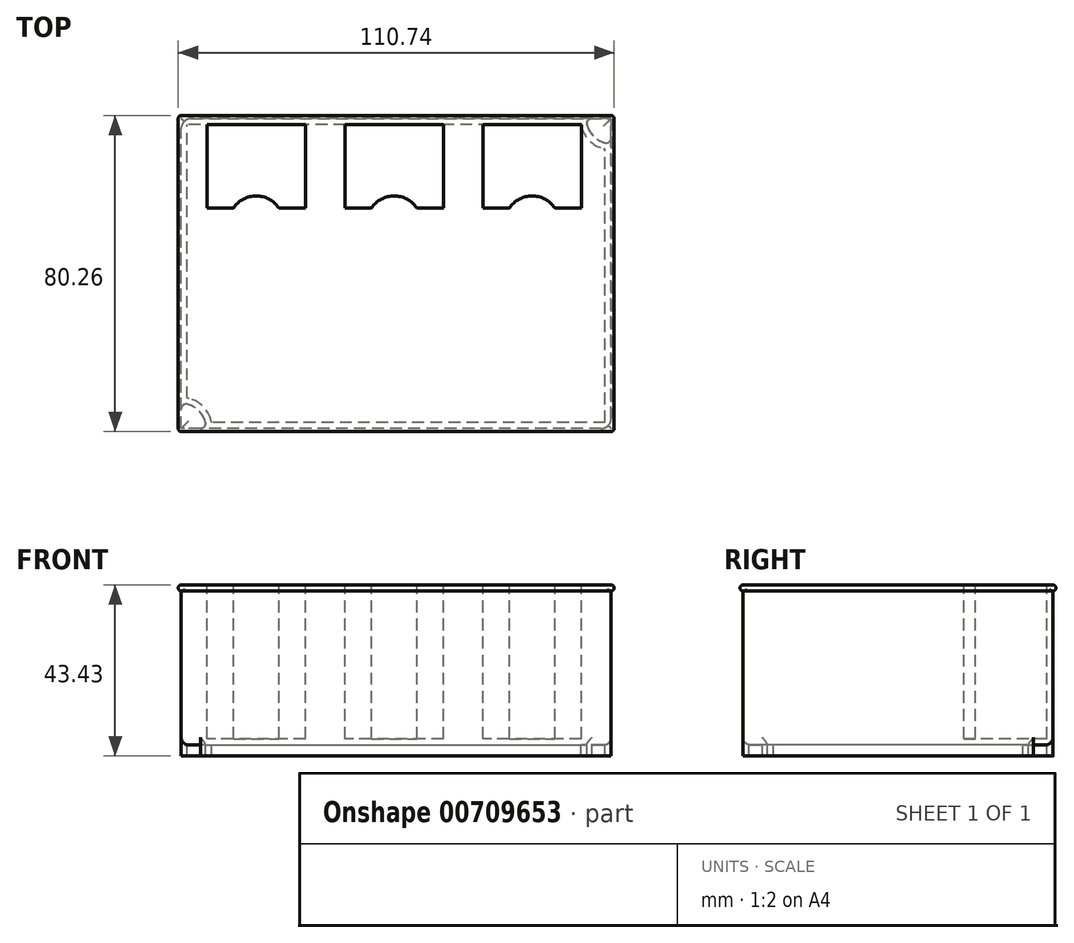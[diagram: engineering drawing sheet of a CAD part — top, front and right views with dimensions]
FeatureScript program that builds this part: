
annotation { "Feature Type Name" : "Feature", "Feature Type Description" : "" }
export const myFeature = defineFeature(function(context is Context, id is Id, definition is map)
    precondition{}
    {
        {
            var Q0;
            Q0=qCreatedBy(makeId("Front.planeOp"),FACE);
            var sketch = newSketch(context, id + "F0", { "sketchPlane" : qUnion([Q0])});
            skLineSegment(sketch, "E0.bottom", {"start": v(54.61, -20.32) * mm, "end": v(-54.61, -20.32) * mm});
            skLineSegment(sketch, "E0.top", {"start": v(54.61, 20.32) * mm, "end": v(-54.61, 20.32) * mm});
            skLineSegment(sketch, "E0.left", {"start": v(54.61, -20.32) * mm, "end": v(54.61, 20.32) * mm});
            skLineSegment(sketch, "E0.right", {"start": v(-54.61, -20.32) * mm, "end": v(-54.61, 20.32) * mm});
            skPoint(sketch, "E0.middle", {"position": v(0, 0) * mm});
            skSolve(sketch);
        }
        {
            var Q0;
            Q0=makeQuery(id+"F0.imprint","IMPRINT",FACE,{"disambiguationData":[TD([[makeQuery(id+"F0.imprint","IMPRINT",EDGE,{"derivedFrom":sQuery(id+"F0.wireOp",EDGE,"E0.bottom")}),-1.0]])]});
            extrude(context, id + "F1", {"entities" : qUnion([Q0]), "depth" : 78.74 * mm, "symmetric" : true});
        }
        {
            var Q0;
            Q0=makeQuery(id+"F1.opExtrude","SWEPT_FACE",FACE,{"disambiguationData":[OSD([sQuery(id+"F0.wireOp",EDGE,"E0.top")])]});
            shell(context, id + "F2", {"entities" : qUnion([Q0]), "thickness" : 1.52 * mm});
        }
        {
            var Q0;
            Q0=makeQuery(id+"F1.opExtrude","CAP_FACE",FACE,{"disambiguationData":[OSD([sQuery(id+"F0.wireOp",EDGE,"E0.bottom"),sQuery(id+"F0.wireOp",EDGE,"E0.top"),sQuery(id+"F0.wireOp",EDGE,"E0.left"),sQuery(id+"F0.wireOp",EDGE,"E0.right")])],"isStart":false});
            var sketch = newSketch(context, id + "F3", { "sketchPlane" : qUnion([Q0])});
            skArc(sketch, "E1", {"start": v(-54.61, 20.32) * mm, "mid": v(-55.37, 19.56) * mm, "end": v(-54.61, 18.8) * mm});
            skSolve(sketch);
        }
        {
            var Q0;
            {var subQ0=sQuery(id+"F3.wireOp",EDGE,"E1");Q0=makeQuery(id+"F3.imprint","IMPRINT",FACE,{"disambiguationData":[TD([[makeQuery(id+"F3.imprint","IMPRINT",EDGE,{"derivedFrom":subQ0}),1.0]])]});}
            var Q1;
            Q1=makeQuery(id+"F1.opExtrude","SWEPT_EDGE",EDGE,{"disambiguationData":[OSD([sQuery(id+"F0.wireOp",EDGE,"E0.top"),sQuery(id+"F0.wireOp",EDGE,"E0.right")])]});
            var Q2;
            Q2=makeQuery(id+"F1.opExtrude","CAP_EDGE",EDGE,{"disambiguationData":[OSD([sQuery(id+"F0.wireOp",EDGE,"E0.top")])],"isStart":true});
            var Q3;
            Q3=makeQuery(id+"F1.opExtrude","SWEPT_EDGE",EDGE,{"disambiguationData":[OSD([sQuery(id+"F0.wireOp",EDGE,"E0.top"),sQuery(id+"F0.wireOp",EDGE,"E0.left")])]});
            var Q4;
            Q4=makeQuery(id+"F1.opExtrude","CAP_EDGE",EDGE,{"disambiguationData":[OSD([sQuery(id+"F0.wireOp",EDGE,"E0.top")])],"isStart":false});
            sweep(context, id + "F4", {"operationType" : NewBodyOperationType.ADD, "profiles" : qUnion([Q0]), "path" : qUnion([Q1, Q2, Q3, Q4])});
        }
        {
            var Q0;
            Q0=makeQuery(id+"F1.opExtrude","SWEPT_FACE",FACE,{"disambiguationData":[OSD([sQuery(id+"F0.wireOp",EDGE,"E0.bottom")])]});
            var sketch = newSketch(context, id + "F5", { "sketchPlane" : qUnion([Q0])});
            skLineSegment(sketch, "E2.bottom", {"start": v(54.61, 39.37) * mm, "end": v(49.7, 39.37) * mm});
            skLineSegment(sketch, "E2.left", {"start": v(54.61, 39.37) * mm, "end": v(54.61, 34.45) * mm});
            skPoint(sketch, "E3.newPointA", {"position": v(48.26, 19.05) * mm});
            skArc(sketch, "E4", {"start": v(48.46, 37.78) * mm, "mid": v(50.12, 34.88) * mm, "end": v(53.02, 33.22) * mm});
            skPoint(sketch, "E5.visualSharp", {"position": v(48.26, 39.37) * mm});
            skArc(sketch, "E5.filletArc", {"start": v(49.7, 39.37) * mm, "mid": v(48.69, 38.88) * mm, "end": v(48.46, 37.78) * mm});
            skPoint(sketch, "E6.visualSharp", {"position": v(54.61, 33.02) * mm});
            skArc(sketch, "E6.filletArc", {"start": v(53.02, 33.22) * mm, "mid": v(54.12, 33.45) * mm, "end": v(54.6, 34.45) * mm});
            skArc(sketch, "E7.MirrorCS", {"start": v(-49.7, 39.37) * mm, "mid": v(-48.69, 38.88) * mm, "end": v(-48.46, 37.78) * mm});
            skArc(sketch, "E8.MirrorCS", {"start": v(-48.46, 37.78) * mm, "mid": v(-50.12, 34.88) * mm, "end": v(-53.02, 33.22) * mm});
            skArc(sketch, "E9.MirrorCS", {"start": v(-53.02, 33.22) * mm, "mid": v(-54.12, 33.45) * mm, "end": v(-54.6, 34.45) * mm});
            skLineSegment(sketch, "E10.MirrorCS", {"start": v(-54.61, 39.37) * mm, "end": v(-54.61, 34.45) * mm});
            skLineSegment(sketch, "E11.MirrorCS", {"start": v(-54.61, 39.37) * mm, "end": v(-49.7, 39.37) * mm});
            skArc(sketch, "E12.MirrorCS", {"start": v(-48.46, -37.78) * mm, "mid": v(-50.12, -34.88) * mm, "end": v(-53.02, -33.22) * mm});
            skArc(sketch, "E13.MirrorCS", {"start": v(-49.7, -39.37) * mm, "mid": v(-48.69, -38.88) * mm, "end": v(-48.46, -37.78) * mm});
            skLineSegment(sketch, "E14.MirrorCS", {"start": v(-54.6, -39.37) * mm, "end": v(-49.7, -39.37) * mm});
            skLineSegment(sketch, "E15.MirrorCS", {"start": v(-54.6, -39.37) * mm, "end": v(-54.6, -34.45) * mm});
            skArc(sketch, "E16.MirrorCS", {"start": v(-53.02, -33.22) * mm, "mid": v(-54.12, -33.45) * mm, "end": v(-54.6, -34.45) * mm});
            skArc(sketch, "E17.MirrorCS", {"start": v(49.7, -39.37) * mm, "mid": v(48.69, -38.88) * mm, "end": v(48.46, -37.78) * mm});
            skArc(sketch, "E18.MirrorCS", {"start": v(48.46, -37.78) * mm, "mid": v(50.12, -34.88) * mm, "end": v(53.02, -33.22) * mm});
            skArc(sketch, "E19.MirrorCS", {"start": v(53.02, -33.22) * mm, "mid": v(54.12, -33.45) * mm, "end": v(54.6, -34.45) * mm});
            skLineSegment(sketch, "E20.MirrorCS", {"start": v(54.6, -39.37) * mm, "end": v(54.6, -34.45) * mm});
            skLineSegment(sketch, "E21.MirrorCS", {"start": v(54.6, -39.37) * mm, "end": v(49.7, -39.37) * mm});
            skSolve(sketch);
        }
        {
            var Q0;
            Q0=makeQuery(id+"F5.imprint","IMPRINT",FACE,{"disambiguationData":[TD([[makeQuery(id+"F5.imprint","IMPRINT",EDGE,{"derivedFrom":sQuery(id+"F5.wireOp",EDGE,"E2.bottom")}),1.0]])]});
            var Q1;
            Q1=makeQuery(id+"F5.imprint","IMPRINT",FACE,{"disambiguationData":[TD([[makeQuery(id+"F5.imprint","IMPRINT",EDGE,{"derivedFrom":sQuery(id+"F5.wireOp",EDGE,"E8.MirrorCS")}),-1.0]])]});
            var Q2;
            Q2=makeQuery(id+"F5.imprint","IMPRINT",FACE,{"disambiguationData":[TD([[makeQuery(id+"F5.imprint","IMPRINT",EDGE,{"derivedFrom":sQuery(id+"F5.wireOp",EDGE,"E12.MirrorCS")}),1.0]])]});
            var Q3;
            Q3=makeQuery(id+"F5.imprint","IMPRINT",FACE,{"disambiguationData":[TD([[makeQuery(id+"F5.imprint","IMPRINT",EDGE,{"derivedFrom":sQuery(id+"F5.wireOp",EDGE,"E17.MirrorCS")}),-1.0]])]});
            extrude(context, id + "F6", {"entities" : qUnion([Q0, Q1, Q2, Q3]), "operationType" : NewBodyOperationType.ADD, "depth" : 2.8 * mm});
        }
        {
            var Q0;
            Q0=makeQuery(id+"F6.opExtrude","CAP_FACE",FACE,{"disambiguationData":[OSD([sQuery(id+"F5.wireOp",EDGE,"E2.bottom"),sQuery(id+"F5.wireOp",EDGE,"E2.left"),sQuery(id+"F5.wireOp",EDGE,"E4"),sQuery(id+"F5.wireOp",EDGE,"E5.filletArc"),sQuery(id+"F5.wireOp",EDGE,"E6.filletArc")])],"isStart":false});
            var Q1;
            Q1=makeQuery(id+"F6.opExtrude","CAP_FACE",FACE,{"disambiguationData":[OSD([sQuery(id+"F5.wireOp",EDGE,"E8.MirrorCS"),sQuery(id+"F5.wireOp",EDGE,"E9.MirrorCS"),sQuery(id+"F5.wireOp",EDGE,"E10.MirrorCS"),sQuery(id+"F5.wireOp",EDGE,"E7.MirrorCS"),sQuery(id+"F5.wireOp",EDGE,"E11.MirrorCS")])],"isStart":false});
            var Q2;
            Q2=makeQuery(id+"F6.opExtrude","CAP_FACE",FACE,{"disambiguationData":[OSD([sQuery(id+"F5.wireOp",EDGE,"E12.MirrorCS"),sQuery(id+"F5.wireOp",EDGE,"E13.MirrorCS"),sQuery(id+"F5.wireOp",EDGE,"E14.MirrorCS"),sQuery(id+"F5.wireOp",EDGE,"E15.MirrorCS"),sQuery(id+"F5.wireOp",EDGE,"E16.MirrorCS")])],"isStart":false});
            var Q3;
            Q3=makeQuery(id+"F6.opExtrude","CAP_FACE",FACE,{"disambiguationData":[OSD([sQuery(id+"F5.wireOp",EDGE,"E17.MirrorCS"),sQuery(id+"F5.wireOp",EDGE,"E18.MirrorCS"),sQuery(id+"F5.wireOp",EDGE,"E19.MirrorCS"),sQuery(id+"F5.wireOp",EDGE,"E20.MirrorCS"),sQuery(id+"F5.wireOp",EDGE,"E21.MirrorCS")])],"isStart":false});
            shell(context, id + "F7", {"entities" : qUnion([Q0, Q1, Q2, Q3]), "thickness" : 1.52 * mm});
        }
        {
            var Q0;
            Q0=makeQuery(id+"F1.opExtrude","SWEPT_EDGE",EDGE,{"disambiguationData":[OSD([sQuery(id+"F0.wireOp",EDGE,"E0.bottom"),sQuery(id+"F0.wireOp",EDGE,"E0.right")])]});
            var Q1;
            Q1=makeQuery(id+"F1.opExtrude","CAP_EDGE",EDGE,{"disambiguationData":[OSD([sQuery(id+"F0.wireOp",EDGE,"E0.bottom")])],"isStart":false});
            var Q2;
            Q2=makeQuery(id+"F1.opExtrude","SWEPT_EDGE",EDGE,{"disambiguationData":[OSD([sQuery(id+"F0.wireOp",EDGE,"E0.bottom"),sQuery(id+"F0.wireOp",EDGE,"E0.left")])]});
            var Q3;
            Q3=makeQuery(id+"F1.opExtrude","CAP_EDGE",EDGE,{"disambiguationData":[OSD([sQuery(id+"F0.wireOp",EDGE,"E0.bottom")])],"isStart":true});
            fillet(context, id + "F8", {"entities" : qUnion([Q0, Q1, Q2, Q3]), "radius" : 1.9 * mm, "tangentPropagation" : true, "allowEdgeOverflow" : false});
        }
        {
            var Q0;
            Q0=makeQuery(id+"F4.opSweep","MID_CAP_EDGE",EDGE,{"disambiguationData":[OSD([sQuery(id+"F0.wireOp",EDGE,"E0.top"),sQuery(id+"F0.wireOp",EDGE,"E0.left"),sQuery(id+"F3.wireOp",EDGE,"E1")])],"capPos":3.0});
            var Q1;
            Q1=makeQuery(id+"F4.opSweep","MID_CAP_EDGE",EDGE,{"disambiguationData":[OSD([sQuery(id+"F0.wireOp",EDGE,"E0.top"),sQuery(id+"F0.wireOp",EDGE,"E0.left"),sQuery(id+"F3.wireOp",EDGE,"E1")])],"capPos":2.0});
            var Q2;
            Q2=makeQuery(id+"F4.opSweep","MID_CAP_EDGE",EDGE,{"disambiguationData":[OSD([sQuery(id+"F0.wireOp",EDGE,"E0.top"),sQuery(id+"F0.wireOp",EDGE,"E0.right"),sQuery(id+"F3.wireOp",EDGE,"E1")])],"capPos":1.0});
            var Q3;
            Q3=makeQuery(id+"F4.opSweep","CAP_EDGE",EDGE,{"disambiguationData":[OSD([sQuery(id+"F0.wireOp",EDGE,"E0.top"),sQuery(id+"F0.wireOp",EDGE,"E0.right"),sQuery(id+"F3.wireOp",EDGE,"E1")])],"isStart":true});
            fillet(context, id + "F9", {"entities" : qUnion([Q0, Q1, Q2, Q3]), "radius" : 0.76 * mm, "tangentPropagation" : true, "allowEdgeOverflow" : false});
        }
        {
            var Q0;
            Q0=makeQuery(id+"F6.boolean.opBoolean","MERGE",EDGE,{"derivedFrom":[makeQuery(id+"F1.opExtrude","CAP_EDGE",EDGE,{"disambiguationData":[OSD([sQuery(id+"F0.wireOp",EDGE,"E0.left")])],"isStart":false}),makeQuery(id+"F6.opExtrude","SWEPT_EDGE",EDGE,{"disambiguationData":[OSD([sQuery(id+"F5.wireOp",EDGE,"E2.bottom"),sQuery(id+"F5.wireOp",EDGE,"E2.left")])]})]});
            var Q1;
            Q1=makeQuery(id+"F6.boolean.opBoolean","MERGE",EDGE,{"derivedFrom":[makeQuery(id+"F1.opExtrude","CAP_EDGE",EDGE,{"disambiguationData":[OSD([sQuery(id+"F0.wireOp",EDGE,"E0.left")])],"isStart":true}),makeQuery(id+"F6.opExtrude","SWEPT_EDGE",EDGE,{"disambiguationData":[OSD([sQuery(id+"F5.wireOp",EDGE,"E20.MirrorCS"),sQuery(id+"F5.wireOp",EDGE,"E21.MirrorCS")])]})]});
            var Q2;
            Q2=makeQuery(id+"F6.boolean.opBoolean","MERGE",EDGE,{"derivedFrom":[makeQuery(id+"F1.opExtrude","CAP_EDGE",EDGE,{"disambiguationData":[OSD([sQuery(id+"F0.wireOp",EDGE,"E0.right")])],"isStart":false}),makeQuery(id+"F6.opExtrude","SWEPT_EDGE",EDGE,{"disambiguationData":[OSD([sQuery(id+"F5.wireOp",EDGE,"E10.MirrorCS"),sQuery(id+"F5.wireOp",EDGE,"E11.MirrorCS")])]})]});
            var Q3;
            Q3=makeQuery(id+"F6.boolean.opBoolean","MERGE",EDGE,{"derivedFrom":[makeQuery(id+"F1.opExtrude","CAP_EDGE",EDGE,{"disambiguationData":[OSD([sQuery(id+"F0.wireOp",EDGE,"E0.right")])],"isStart":true}),makeQuery(id+"F6.opExtrude","SWEPT_EDGE",EDGE,{"disambiguationData":[OSD([sQuery(id+"F5.wireOp",EDGE,"E14.MirrorCS"),sQuery(id+"F5.wireOp",EDGE,"E15.MirrorCS")])]})]});
            fillet(context, id + "F10", {"entities" : qUnion([Q0, Q1, Q2, Q3]), "radius" : 2.54 * mm, "tangentPropagation" : true, "allowEdgeOverflow" : false});
        }
        {
            var Q0;
            Q0=makeQuery(id+"F1.opExtrude","SWEPT_FACE",FACE,{"disambiguationData":[OSD([sQuery(id+"F0.wireOp",EDGE,"E0.top")])]});
            var sketch = newSketch(context, id + "F11", { "sketchPlane" : qUnion([Q0])});
            skLineSegment(sketch, "E22.0", {"start": v(-53.09, -12.45) * mm, "end": v(-53.09, 37.85) * mm});
            skLineSegment(sketch, "E22.1", {"start": v(-53.09, 37.85) * mm, "end": v(-18.03, 37.85) * mm});
            skLineSegment(sketch, "E23", {"start": v(-18.03, 37.85) * mm, "end": v(-23.03, 37.85) * mm});
            skLineSegment(sketch, "E24", {"start": v(-23.03, 37.85) * mm, "end": v(-23.03, 16.7) * mm});
            skLineSegment(sketch, "E25", {"start": v(-53.09, 37.85) * mm, "end": v(-48.09, 37.85) * mm});
            skLineSegment(sketch, "E26", {"start": v(-48.09, 37.85) * mm, "end": v(-48.09, 16.7) * mm});
            skLineSegment(sketch, "E27.left", {"start": v(-23.03, 16.7) * mm, "end": v(-29.82, 16.7) * mm});
            skLineSegment(sketch, "E27.right", {"start": v(-23.03, 8.7) * mm, "end": v(-29.82, 8.7) * mm});
            skPoint(sketch, "E27.middle", {"position": v(-35.56, 12.7) * mm});
            skArc(sketch, "E28", {"start": v(-29.82, 16.7) * mm, "mid": v(-35.56, 19.7) * mm, "end": v(-41.3, 16.7) * mm});
            skLineSegment(sketch, "E29.bottom", {"start": v(-33.31, -0.3) * mm, "end": v(-33.31, 6.07) * mm});
            skLineSegment(sketch, "E29.top", {"start": v(-37.81, -0.3) * mm, "end": v(-37.81, 6.07) * mm});
            skLineSegment(sketch, "E29.left", {"start": v(-33.31, -0.3) * mm, "end": v(-37.81, -0.3) * mm});
            skLineSegment(sketch, "E30.trimOffspring", {"start": v(-41.3, 8.7) * mm, "end": v(-47.07, 8.7) * mm});
            skLineSegment(sketch, "E31.trimOffspring", {"start": v(-41.3, 16.7) * mm, "end": v(-48.09, 16.7) * mm});
            skArc(sketch, "E32.trimOffspring", {"start": v(-41.3, 8.7) * mm, "mid": v(-39.77, 7.1) * mm, "end": v(-37.81, 6.07) * mm});
            skLineSegment(sketch, "E33.trimOffspring", {"start": v(-23.03, 8.7) * mm, "end": v(-23.03, -8.7) * mm});
            skArc(sketch, "E34.trimOffspring", {"start": v(-33.31, 6.07) * mm, "mid": v(-31.35, 7.1) * mm, "end": v(-29.82, 8.7) * mm});
            skPoint(sketch, "E35", {"position": v(-20.53, -12.45) * mm});
            skLineSegment(sketch, "E36.1", {"start": v(-18.03, 37.85) * mm, "end": v(17.02, 37.85) * mm});
            skLineSegment(sketch, "E37", {"start": v(17.02, 37.85) * mm, "end": v(12.02, 37.85) * mm});
            skLineSegment(sketch, "E38", {"start": v(12.02, 37.85) * mm, "end": v(12.02, 16.7) * mm});
            skLineSegment(sketch, "E39", {"start": v(-18.03, 37.85) * mm, "end": v(-13.03, 37.85) * mm});
            skLineSegment(sketch, "E40", {"start": v(-13.03, 37.85) * mm, "end": v(-13.03, 16.7) * mm});
            skLineSegment(sketch, "E41.left", {"start": v(12.02, 16.7) * mm, "end": v(5.24, 16.7) * mm});
            skLineSegment(sketch, "E41.right", {"start": v(12.02, 8.7) * mm, "end": v(5.24, 8.7) * mm});
            skPoint(sketch, "E41.middle", {"position": v(-0.5, 12.7) * mm});
            skArc(sketch, "E42", {"start": v(5.24, 16.7) * mm, "mid": v(-0.5, 19.7) * mm, "end": v(-6.25, 16.7) * mm});
            skLineSegment(sketch, "E43.bottom", {"start": v(1.74, -0.3) * mm, "end": v(1.74, 6.07) * mm});
            skLineSegment(sketch, "E43.top", {"start": v(-2.76, -0.3) * mm, "end": v(-2.76, 6.07) * mm});
            skLineSegment(sketch, "E43.left", {"start": v(1.74, -0.3) * mm, "end": v(-2.76, -0.3) * mm});
            skLineSegment(sketch, "E44.trimOffspring", {"start": v(-6.25, 8.7) * mm, "end": v(-12.02, 8.7) * mm});
            skLineSegment(sketch, "E45.trimOffspring", {"start": v(-6.25, 16.7) * mm, "end": v(-13.03, 16.7) * mm});
            skArc(sketch, "E46.trimOffspring", {"start": v(-6.25, 8.7) * mm, "mid": v(-4.72, 7.1) * mm, "end": v(-2.76, 6.07) * mm});
            skLineSegment(sketch, "E47.trimOffspring", {"start": v(12.02, 8.7) * mm, "end": v(12.02, -8.7) * mm});
            skArc(sketch, "E48.trimOffspring", {"start": v(1.74, 6.07) * mm, "mid": v(3.7, 7.1) * mm, "end": v(5.24, 8.7) * mm});
            skPoint(sketch, "E49", {"position": v(14.52, -12.45) * mm});
            skLineSegment(sketch, "E50.1", {"start": v(17.02, 37.85) * mm, "end": v(52.07, 37.85) * mm});
            skLineSegment(sketch, "E50.2", {"start": v(52.07, 12.45) * mm, "end": v(52.07, 37.85) * mm});
            skLineSegment(sketch, "E51", {"start": v(52.07, 37.85) * mm, "end": v(47.07, 37.85) * mm});
            skLineSegment(sketch, "E52", {"start": v(47.07, 37.85) * mm, "end": v(47.07, 16.7) * mm});
            skLineSegment(sketch, "E53", {"start": v(17.02, 37.85) * mm, "end": v(22.02, 37.85) * mm});
            skLineSegment(sketch, "E54", {"start": v(22.02, 37.85) * mm, "end": v(22.02, 16.7) * mm});
            skLineSegment(sketch, "E55.left", {"start": v(47.07, 16.7) * mm, "end": v(40.29, 16.7) * mm});
            skLineSegment(sketch, "E55.right", {"start": v(47.07, 8.7) * mm, "end": v(40.29, 8.7) * mm});
            skPoint(sketch, "E55.middle", {"position": v(34.54, 12.7) * mm});
            skArc(sketch, "E56", {"start": v(40.29, 16.7) * mm, "mid": v(34.54, 19.7) * mm, "end": v(28.8, 16.7) * mm});
            skLineSegment(sketch, "E57.bottom", {"start": v(36.8, -0.3) * mm, "end": v(36.8, 6.07) * mm});
            skLineSegment(sketch, "E57.top", {"start": v(32.3, -0.3) * mm, "end": v(32.3, 6.07) * mm});
            skLineSegment(sketch, "E57.left", {"start": v(36.8, -0.3) * mm, "end": v(32.3, -0.3) * mm});
            skLineSegment(sketch, "E58.trimOffspring", {"start": v(28.8, 8.7) * mm, "end": v(23.03, 8.7) * mm});
            skLineSegment(sketch, "E59.trimOffspring", {"start": v(28.8, 16.7) * mm, "end": v(22.02, 16.7) * mm});
            skArc(sketch, "E60.trimOffspring", {"start": v(28.8, 8.7) * mm, "mid": v(30.34, 7.1) * mm, "end": v(32.3, 6.07) * mm});
            skLineSegment(sketch, "E61.trimOffspring", {"start": v(47.07, 8.7) * mm, "end": v(47.07, -8.7) * mm});
            skArc(sketch, "E62.trimOffspring", {"start": v(36.8, 6.07) * mm, "mid": v(38.75, 7.1) * mm, "end": v(40.29, 8.7) * mm});
            skPoint(sketch, "E63", {"position": v(49.57, -12.45) * mm});
            skLineSegment(sketch, "E64.0", {"start": v(-52.07, -37.85) * mm, "end": v(-52.07, -12.45) * mm});
            skLineSegment(sketch, "E64.3", {"start": v(-52.07, -37.85) * mm, "end": v(-17.02, -37.85) * mm});
            skLineSegment(sketch, "E65", {"start": v(-47.07, 8.7) * mm, "end": v(-47.07, -8.7) * mm});
            skLineSegment(sketch, "E66.left", {"start": v(-23.03, -8.7) * mm, "end": v(-28.8, -8.7) * mm});
            skLineSegment(sketch, "E66.right", {"start": v(-22.02, -16.7) * mm, "end": v(-28.8, -16.7) * mm});
            skPoint(sketch, "E66.middle", {"position": v(-34.54, -12.7) * mm});
            skArc(sketch, "E67", {"start": v(-28.8, -8.7) * mm, "mid": v(-34.54, -5.7) * mm, "end": v(-40.29, -8.7) * mm});
            skLineSegment(sketch, "E68.bottom", {"start": v(-32.3, -25.7) * mm, "end": v(-32.3, -19.33) * mm});
            skLineSegment(sketch, "E68.top", {"start": v(-36.8, -25.7) * mm, "end": v(-36.8, -19.33) * mm});
            skLineSegment(sketch, "E68.left", {"start": v(-32.3, -25.7) * mm, "end": v(-36.8, -25.7) * mm});
            skLineSegment(sketch, "E69.trimOffspring", {"start": v(-40.29, -16.7) * mm, "end": v(-47.07, -16.7) * mm});
            skLineSegment(sketch, "E70.trimOffspring", {"start": v(-40.29, -8.7) * mm, "end": v(-47.07, -8.7) * mm});
            skArc(sketch, "E71.trimOffspring", {"start": v(-40.29, -16.7) * mm, "mid": v(-38.75, -18.3) * mm, "end": v(-36.8, -19.33) * mm});
            skLineSegment(sketch, "E72.trimOffspring", {"start": v(-47.07, -16.7) * mm, "end": v(-47.07, -37.85) * mm});
            skLineSegment(sketch, "E73.trimOffspring", {"start": v(-22.02, -16.7) * mm, "end": v(-22.02, -37.85) * mm});
            skArc(sketch, "E74.trimOffspring", {"start": v(-32.3, -19.33) * mm, "mid": v(-30.34, -18.3) * mm, "end": v(-28.8, -16.7) * mm});
            skLineSegment(sketch, "E75", {"start": v(-22.02, -37.85) * mm, "end": v(-17.02, -37.85) * mm});
            skPoint(sketch, "E76", {"position": v(-19.52, -37.85) * mm});
            skLineSegment(sketch, "E77.3", {"start": v(-17.02, -37.85) * mm, "end": v(18.03, -37.85) * mm});
            skLineSegment(sketch, "E78", {"start": v(-12.02, 8.7) * mm, "end": v(-12.02, -8.7) * mm});
            skLineSegment(sketch, "E79.left", {"start": v(12.02, -8.7) * mm, "end": v(6.25, -8.7) * mm});
            skLineSegment(sketch, "E79.right", {"start": v(13.03, -16.7) * mm, "end": v(6.25, -16.7) * mm});
            skPoint(sketch, "E79.middle", {"position": v(0.5, -12.7) * mm});
            skArc(sketch, "E80", {"start": v(6.25, -8.7) * mm, "mid": v(0.5, -5.7) * mm, "end": v(-5.24, -8.7) * mm});
            skLineSegment(sketch, "E81.bottom", {"start": v(2.76, -25.7) * mm, "end": v(2.76, -19.33) * mm});
            skLineSegment(sketch, "E81.top", {"start": v(-1.74, -25.7) * mm, "end": v(-1.74, -19.33) * mm});
            skLineSegment(sketch, "E81.left", {"start": v(2.76, -25.7) * mm, "end": v(-1.74, -25.7) * mm});
            skLineSegment(sketch, "E82.trimOffspring", {"start": v(-5.24, -16.7) * mm, "end": v(-12.02, -16.7) * mm});
            skLineSegment(sketch, "E83.trimOffspring", {"start": v(-5.24, -8.7) * mm, "end": v(-12.02, -8.7) * mm});
            skArc(sketch, "E84.trimOffspring", {"start": v(-5.24, -16.7) * mm, "mid": v(-3.7, -18.3) * mm, "end": v(-1.74, -19.33) * mm});
            skLineSegment(sketch, "E85.trimOffspring", {"start": v(-12.02, -16.7) * mm, "end": v(-12.02, -37.85) * mm});
            skLineSegment(sketch, "E86.trimOffspring", {"start": v(13.03, -16.7) * mm, "end": v(13.03, -37.85) * mm});
            skArc(sketch, "E87.trimOffspring", {"start": v(2.76, -19.33) * mm, "mid": v(4.72, -18.3) * mm, "end": v(6.25, -16.7) * mm});
            skLineSegment(sketch, "E88", {"start": v(13.03, -37.85) * mm, "end": v(18.03, -37.85) * mm});
            skPoint(sketch, "E89", {"position": v(15.53, -37.85) * mm});
            skLineSegment(sketch, "E90.2", {"start": v(53.09, -37.85) * mm, "end": v(53.09, 12.45) * mm});
            skLineSegment(sketch, "E90.3", {"start": v(18.03, -37.85) * mm, "end": v(53.09, -37.85) * mm});
            skLineSegment(sketch, "E91", {"start": v(53.09, 12.45) * mm, "end": v(52.07, 12.45) * mm});
            skLineSegment(sketch, "E92", {"start": v(23.03, 8.7) * mm, "end": v(23.03, -8.7) * mm});
            skLineSegment(sketch, "E93.left", {"start": v(47.07, -8.7) * mm, "end": v(41.3, -8.7) * mm});
            skLineSegment(sketch, "E93.right", {"start": v(48.09, -16.7) * mm, "end": v(41.3, -16.7) * mm});
            skPoint(sketch, "E93.middle", {"position": v(35.56, -12.7) * mm});
            skArc(sketch, "E94", {"start": v(41.3, -8.7) * mm, "mid": v(35.56, -5.7) * mm, "end": v(29.82, -8.7) * mm});
            skLineSegment(sketch, "E95.bottom", {"start": v(37.81, -25.7) * mm, "end": v(37.81, -19.33) * mm});
            skLineSegment(sketch, "E95.top", {"start": v(33.31, -25.7) * mm, "end": v(33.31, -19.33) * mm});
            skLineSegment(sketch, "E95.left", {"start": v(37.81, -25.7) * mm, "end": v(33.31, -25.7) * mm});
            skLineSegment(sketch, "E96.trimOffspring", {"start": v(29.82, -16.7) * mm, "end": v(23.03, -16.7) * mm});
            skLineSegment(sketch, "E97.trimOffspring", {"start": v(29.82, -8.7) * mm, "end": v(23.03, -8.7) * mm});
            skArc(sketch, "E98.trimOffspring", {"start": v(29.82, -16.7) * mm, "mid": v(31.35, -18.3) * mm, "end": v(33.31, -19.33) * mm});
            skLineSegment(sketch, "E99.trimOffspring", {"start": v(23.03, -16.7) * mm, "end": v(23.03, -37.85) * mm});
            skLineSegment(sketch, "E100.trimOffspring", {"start": v(48.09, -16.7) * mm, "end": v(48.09, -37.85) * mm});
            skArc(sketch, "E101.trimOffspring", {"start": v(37.81, -19.33) * mm, "mid": v(39.77, -18.3) * mm, "end": v(41.3, -16.7) * mm});
            skLineSegment(sketch, "E102", {"start": v(48.09, -37.85) * mm, "end": v(53.09, -37.85) * mm});
            skPoint(sketch, "E103", {"position": v(50.59, -37.85) * mm});
            skLineSegment(sketch, "E104", {"start": v(-53.09, -12.45) * mm, "end": v(-52.07, -12.45) * mm});
            skPoint(sketch, "E105.orphan", {"position": v(-48.09, 8.7) * mm});
            skPoint(sketch, "E106.orphan", {"position": v(22.02, 8.7) * mm});
            skPoint(sketch, "E107.orphan", {"position": v(48.09, -8.7) * mm});
            skPoint(sketch, "E108.orphan", {"position": v(13.03, -8.7) * mm});
            skPoint(sketch, "E109.orphan", {"position": v(-22.02, -8.7) * mm});
            skPoint(sketch, "E110.orphan", {"position": v(-13.03, 8.7) * mm});
            skSolve(sketch);
        }
        {
            var Q0;
            Q0=makeQuery(id+"F11.imprint","IMPRINT",FACE,{"disambiguationData":[TD([[makeQuery(id+"F11.imprint","IMPRINT",EDGE,{"derivedFrom":sQuery(id+"F11.wireOp",EDGE,"E22.1")}),1.0]])]});
            var Q1;
            Q1=makeQuery(id+"F11.imprint","IMPRINT",FACE,{"disambiguationData":[TD([[makeQuery(id+"F11.imprint","IMPRINT",EDGE,{"derivedFrom":sQuery(id+"F11.wireOp",EDGE,"E36.1")}),1.0]])]});
            var Q2;
            Q2=makeQuery(id+"F11.imprint","IMPRINT",FACE,{"disambiguationData":[TD([[makeQuery(id+"F11.imprint","IMPRINT",EDGE,{"derivedFrom":sQuery(id+"F11.wireOp",EDGE,"E50.1")}),1.0]])]});
            var Q3;
            Q3=makeQuery(id+"F11.imprint","IMPRINT",FACE,{"disambiguationData":[TD([[makeQuery(id+"F11.imprint","IMPRINT",EDGE,{"derivedFrom":sQuery(id+"F11.wireOp",EDGE,"E55.right")}),1.0]])]});
            var Q4;
            Q4=makeQuery(id+"F11.imprint","IMPRINT",FACE,{"disambiguationData":[TD([[makeQuery(id+"F11.imprint","IMPRINT",EDGE,{"derivedFrom":sQuery(id+"F11.wireOp",EDGE,"E93.right")}),1.0]])]});
            var Q5;
            Q5=makeQuery(id+"F11.imprint","IMPRINT",FACE,{"disambiguationData":[TD([[makeQuery(id+"F11.imprint","IMPRINT",EDGE,{"derivedFrom":sQuery(id+"F11.wireOp",EDGE,"E79.right")}),1.0]])]});
            var Q6;
            Q6=makeQuery(id+"F11.imprint","IMPRINT",FACE,{"disambiguationData":[TD([[makeQuery(id+"F11.imprint","IMPRINT",EDGE,{"derivedFrom":sQuery(id+"F11.wireOp",EDGE,"E41.right")}),1.0]])]});
            var Q7;
            Q7=makeQuery(id+"F11.imprint","IMPRINT",FACE,{"disambiguationData":[TD([[makeQuery(id+"F11.imprint","IMPRINT",EDGE,{"derivedFrom":sQuery(id+"F11.wireOp",EDGE,"E27.right")}),1.0]])]});
            var Q8;
            Q8=makeQuery(id+"F11.imprint","IMPRINT",FACE,{"disambiguationData":[TD([[makeQuery(id+"F11.imprint","IMPRINT",EDGE,{"derivedFrom":sQuery(id+"F11.wireOp",EDGE,"E66.right")}),1.0]])]});
            var Q9;
            {var subQ0=sQuery(id+"F11.wireOp",EDGE,"E50.2");Q9=makeQuery(id+"F11.imprint","IMPRINT",FACE,{"disambiguationData":[TD([[makeQuery(id+"F11.imprint","IMPRINT",EDGE,{"derivedFrom":subQ0}),-1.0]])]});}
            var Q10;
            {var subQ0=sQuery(id+"F11.wireOp",EDGE,"E64.0");Q10=makeQuery(id+"F11.imprint","IMPRINT",FACE,{"disambiguationData":[TD([[makeQuery(id+"F11.imprint","IMPRINT",EDGE,{"derivedFrom":subQ0}),1.0]])]});}
            var Q11;
            Q11=makeQuery(id+"F2.opShell","OFFSET_FACE",FACE,{"disambiguationData":[OSD([sQuery(id+"F0.wireOp",EDGE,"E0.bottom")])]});
            extrude(context, id + "F12", {"entities" : qUnion([Q0, Q1, Q2, Q3, Q4, Q5, Q6, Q7, Q8, Q9, Q10]), "operationType" : NewBodyOperationType.ADD, "endBound" : BoundingType.UP_TO_SURFACE, "oppositeDirection" : true, "depth" : 25 * mm, "endBoundEntityFace" : qUnion([Q11]), "offsetDistance" : 25 * mm});
        }
        {
            var Q0;
            {var subQ0=sQuery(id+"F0.wireOp",EDGE,"E0.top");Q0=makeQuery(id+"F12.boolean.opBoolean","MERGE",FACE,{"derivedFrom":[makeQuery(id+"F1.opExtrude","SWEPT_FACE",FACE,{"disambiguationData":[OSD([subQ0])]}),makeQuery(id+"F12.opExtrude","CAP_FACE",FACE,{"disambiguationData":[OSD([sQuery(id+"F11.wireOp",EDGE,"E22.1"),sQuery(id+"F11.wireOp",EDGE,"E24"),sQuery(id+"F11.wireOp",EDGE,"E26"),sQuery(id+"F11.wireOp",EDGE,"E27.left"),sQuery(id+"F11.wireOp",EDGE,"E28"),sQuery(id+"F11.wireOp",EDGE,"E31.trimOffspring")])],"isStart":true}),makeQuery(id+"F12.opExtrude","CAP_FACE",FACE,{"disambiguationData":[OSD([sQuery(id+"F11.wireOp",EDGE,"E36.1"),sQuery(id+"F11.wireOp",EDGE,"E38"),sQuery(id+"F11.wireOp",EDGE,"E40"),sQuery(id+"F11.wireOp",EDGE,"E41.left"),sQuery(id+"F11.wireOp",EDGE,"E42"),sQuery(id+"F11.wireOp",EDGE,"E45.trimOffspring")])],"isStart":true}),makeQuery(id+"F12.opExtrude","CAP_FACE",FACE,{"disambiguationData":[OSD([sQuery(id+"F11.wireOp",EDGE,"E50.1"),sQuery(id+"F11.wireOp",EDGE,"E52"),sQuery(id+"F11.wireOp",EDGE,"E54"),sQuery(id+"F11.wireOp",EDGE,"E55.left"),sQuery(id+"F11.wireOp",EDGE,"E56"),sQuery(id+"F11.wireOp",EDGE,"E59.trimOffspring")])],"isStart":true}),makeQuery(id+"F12.opExtrude","CAP_FACE",FACE,{"disambiguationData":[OSD([subQ0,sQuery(id+"F0.wireOp",EDGE,"E0.left"),sQuery(id+"F11.wireOp",EDGE,"E50.2"),sQuery(id+"F11.wireOp",EDGE,"E91")])],"isStart":true}),makeQuery(id+"F12.opExtrude","CAP_FACE",FACE,{"disambiguationData":[OSD([subQ0,sQuery(id+"F0.wireOp",EDGE,"E0.right"),sQuery(id+"F11.wireOp",EDGE,"E64.0"),sQuery(id+"F11.wireOp",EDGE,"E104")])],"isStart":true}),makeQuery(id+"F12.opExtrude","CAP_FACE",FACE,{"disambiguationData":[OSD([sQuery(id+"F11.wireOp",EDGE,"E64.3"),sQuery(id+"F11.wireOp",EDGE,"E66.right"),sQuery(id+"F11.wireOp",EDGE,"E68.bottom"),sQuery(id+"F11.wireOp",EDGE,"E68.top"),sQuery(id+"F11.wireOp",EDGE,"E68.left"),sQuery(id+"F11.wireOp",EDGE,"E69.trimOffspring"),sQuery(id+"F11.wireOp",EDGE,"E71.trimOffspring"),sQuery(id+"F11.wireOp",EDGE,"E72.trimOffspring"),sQuery(id+"F11.wireOp",EDGE,"E73.trimOffspring"),sQuery(id+"F11.wireOp",EDGE,"E74.trimOffspring")])],"isStart":true}),makeQuery(id+"F12.opExtrude","CAP_FACE",FACE,{"disambiguationData":[OSD([sQuery(id+"F11.wireOp",EDGE,"E77.3"),sQuery(id+"F11.wireOp",EDGE,"E79.right"),sQuery(id+"F11.wireOp",EDGE,"E81.bottom"),sQuery(id+"F11.wireOp",EDGE,"E81.top"),sQuery(id+"F11.wireOp",EDGE,"E81.left"),sQuery(id+"F11.wireOp",EDGE,"E82.trimOffspring"),sQuery(id+"F11.wireOp",EDGE,"E84.trimOffspring"),sQuery(id+"F11.wireOp",EDGE,"E85.trimOffspring"),sQuery(id+"F11.wireOp",EDGE,"E86.trimOffspring"),sQuery(id+"F11.wireOp",EDGE,"E87.trimOffspring")])],"isStart":true}),makeQuery(id+"F12.opExtrude","CAP_FACE",FACE,{"disambiguationData":[OSD([sQuery(id+"F11.wireOp",EDGE,"E90.3"),sQuery(id+"F11.wireOp",EDGE,"E93.right"),sQuery(id+"F11.wireOp",EDGE,"E95.bottom"),sQuery(id+"F11.wireOp",EDGE,"E95.top"),sQuery(id+"F11.wireOp",EDGE,"E95.left"),sQuery(id+"F11.wireOp",EDGE,"E96.trimOffspring"),sQuery(id+"F11.wireOp",EDGE,"E98.trimOffspring"),sQuery(id+"F11.wireOp",EDGE,"E99.trimOffspring"),sQuery(id+"F11.wireOp",EDGE,"E100.trimOffspring"),sQuery(id+"F11.wireOp",EDGE,"E101.trimOffspring")])],"isStart":true})]});}
            var sketch = newSketch(context, id + "F13", { "sketchPlane" : qUnion([Q0])});
            skPoint(sketch, "E111", {"position": v(0.5, -32.53) * mm});
            skCircle(sketch, "E112", {"center": v(0.5, -32.53) * mm, "radius": 6.5 * mm});
            skArc(sketch, "E113", {"start": v(0.5, -39.03) * mm, "mid": v(7, -32.53) * mm, "end": v(0.5, -26.03) * mm});
            skArc(sketch, "E114", {"start": v(1.83, -27.6) * mm, "mid": v(1.32, -27.5) * mm, "end": v(0.8, -27.44) * mm});
            skArc(sketch, "E115", {"start": v(1.66, -36.82) * mm, "mid": v(2.73, -36.38) * mm, "end": v(3.65, -35.67) * mm});
            skPoint(sketch, "E116.startSnap0", {"position": v(0.5, -26.05) * mm});
            skLineSegment(sketch, "E117", {"start": v(0.8, -26.7) * mm, "end": v(0.8, -27.44) * mm});
            skArc(sketch, "E118.trimOffspring", {"start": v(5.43, -31.22) * mm, "mid": v(5.28, -30.72) * mm, "end": v(5.07, -30.25) * mm});
            skArc(sketch, "E119.trimOffspring", {"start": v(4.11, -36.14) * mm, "mid": v(4.46, -35.76) * mm, "end": v(4.77, -35.34) * mm});
            skLineSegment(sketch, "E120.trimOffspring", {"start": v(0.8, -27.44) * mm, "end": v(0.8, -26.7) * mm});
            skLineSegment(sketch, "E121.trimOffspring", {"start": v(4.77, -29.73) * mm, "end": v(5.4, -29.37) * mm});
            skLineSegment(sketch, "E122.trimOffspring", {"start": v(5.07, -30.25) * mm, "end": v(5.7, -29.89) * mm});
            skArc(sketch, "E123.trimOffspring", {"start": v(5.4, -29.37) * mm, "mid": v(3.42, -27.5) * mm, "end": v(0.8, -26.72) * mm});
            skArc(sketch, "E124.trimOffspring", {"start": v(4.77, -29.73) * mm, "mid": v(4.46, -29.31) * mm, "end": v(4.11, -28.93) * mm});
            skLineSegment(sketch, "E125.trimOffspring", {"start": v(5.07, -34.82) * mm, "end": v(5.7, -35.18) * mm});
            skLineSegment(sketch, "E126.trimOffspring", {"start": v(4.77, -35.34) * mm, "end": v(5.4, -35.7) * mm});
            skArc(sketch, "E127.trimOffspring", {"start": v(5.07, -34.82) * mm, "mid": v(5.28, -34.35) * mm, "end": v(5.43, -33.85) * mm});
            skArc(sketch, "E128.trimOffspring", {"start": v(5.7, -35.18) * mm, "mid": v(6.33, -32.53) * mm, "end": v(5.7, -29.89) * mm});
            skLineSegment(sketch, "E129", {"start": v(0.8, -38.36) * mm, "end": v(0.8, -37.63) * mm});
            skArc(sketch, "E130.trimOffspring", {"start": v(0.8, -37.63) * mm, "mid": v(1.32, -37.57) * mm, "end": v(1.83, -37.46) * mm});
            skArc(sketch, "E131.trimOffspring", {"start": v(0.8, -38.35) * mm, "mid": v(3.42, -37.58) * mm, "end": v(5.4, -35.7) * mm});
            skLineSegment(sketch, "E132.trimOffspring", {"start": v(3.65, -35.67) * mm, "end": v(4.11, -36.14) * mm});
            skArc(sketch, "E133.trimOffspring", {"start": v(4.8, -33.68) * mm, "mid": v(4.95, -32.53) * mm, "end": v(4.8, -31.39) * mm});
            skArc(sketch, "E134.trimOffspring", {"start": v(3.65, -29.4) * mm, "mid": v(2.73, -28.7) * mm, "end": v(1.66, -28.25) * mm});
            skLineSegment(sketch, "E135.trimOffspring", {"start": v(4.8, -31.39) * mm, "end": v(5.43, -31.22) * mm});
            skLineSegment(sketch, "E136.trimOffspring", {"start": v(3.65, -29.4) * mm, "end": v(4.11, -28.93) * mm});
            skLineSegment(sketch, "E137.trimOffspring", {"start": v(1.66, -28.25) * mm, "end": v(1.83, -27.6) * mm});
            skLineSegment(sketch, "E138", {"start": v(0.87, -30.66) * mm, "end": v(1.26, -28.67) * mm});
            skLineSegment(sketch, "E139", {"start": v(1.26, -28.67) * mm, "end": v(0.5, -28.67) * mm});
            skLineSegment(sketch, "E140", {"start": v(1.95, -31.28) * mm, "end": v(3.48, -29.95) * mm});
            skLineSegment(sketch, "E141", {"start": v(2.32, -31.91) * mm, "end": v(4.23, -31.25) * mm});
            skLineSegment(sketch, "E142", {"start": v(2.32, -33.16) * mm, "end": v(4.23, -33.82) * mm});
            skLineSegment(sketch, "E143", {"start": v(0.87, -34.41) * mm, "end": v(1.26, -36.4) * mm});
            skLineSegment(sketch, "E144", {"start": v(3.48, -29.95) * mm, "end": v(3.86, -30.6) * mm});
            skLineSegment(sketch, "E145", {"start": v(3.86, -30.6) * mm, "end": v(4.23, -31.25) * mm});
            skLineSegment(sketch, "E146", {"start": v(4.23, -33.82) * mm, "end": v(3.48, -35.12) * mm});
            skLineSegment(sketch, "E147", {"start": v(1.26, -36.4) * mm, "end": v(0.5, -36.4) * mm});
            skLineSegment(sketch, "E148.trimOffspring", {"start": v(1.66, -36.82) * mm, "end": v(1.83, -37.46) * mm});
            skLineSegment(sketch, "E149.trimOffspring", {"start": v(4.8, -33.68) * mm, "end": v(5.43, -33.85) * mm});
            skArc(sketch, "E150.trimOffspring", {"start": v(1.95, -31.28) * mm, "mid": v(1.46, -30.88) * mm, "end": v(0.87, -30.66) * mm});
            skArc(sketch, "E151.trimOffspring", {"start": v(0.87, -34.41) * mm, "mid": v(1.46, -34.2) * mm, "end": v(1.95, -33.79) * mm});
            skLineSegment(sketch, "E152", {"start": v(3.48, -35.12) * mm, "end": v(1.95, -33.79) * mm});
            skArc(sketch, "E153.trimOffspring", {"start": v(2.32, -33.16) * mm, "mid": v(2.42, -32.53) * mm, "end": v(2.32, -31.91) * mm});
            skLineSegment(sketch, "E154.MirrorCS", {"start": v(0.2, -26.7) * mm, "end": v(0.2, -27.44) * mm});
            skLineSegment(sketch, "E155.MirrorCS", {"start": v(0.2, -27.44) * mm, "end": v(0.2, -26.7) * mm});
            skLineSegment(sketch, "E156.MirrorCS", {"start": v(-3.78, -31.39) * mm, "end": v(-4.42, -31.22) * mm});
            skLineSegment(sketch, "E157.MirrorCS", {"start": v(-2.84, -30.6) * mm, "end": v(-3.21, -31.25) * mm});
            skLineSegment(sketch, "E158.MirrorCS", {"start": v(-2.63, -29.4) * mm, "end": v(-3.1, -28.93) * mm});
            skLineSegment(sketch, "E159.MirrorCS", {"start": v(-4.05, -30.25) * mm, "end": v(-4.68, -29.89) * mm});
            skLineSegment(sketch, "E160.MirrorCS", {"start": v(-0.64, -28.25) * mm, "end": v(-0.81, -27.6) * mm});
            skLineSegment(sketch, "E161.MirrorCS", {"start": v(-2.46, -29.95) * mm, "end": v(-2.84, -30.6) * mm});
            skLineSegment(sketch, "E162.MirrorCS", {"start": v(-3.75, -35.34) * mm, "end": v(-4.38, -35.7) * mm});
            skLineSegment(sketch, "E163.MirrorCS", {"start": v(-3.75, -29.73) * mm, "end": v(-4.38, -29.37) * mm});
            skLineSegment(sketch, "E164.MirrorCS", {"start": v(0.2, -38.36) * mm, "end": v(0.2, -37.63) * mm});
            skLineSegment(sketch, "E165.MirrorCS", {"start": v(-2.63, -35.67) * mm, "end": v(-3.1, -36.14) * mm});
            skLineSegment(sketch, "E166.MirrorCS", {"start": v(-0.64, -36.82) * mm, "end": v(-0.81, -37.46) * mm});
            skLineSegment(sketch, "E167.MirrorCS", {"start": v(-3.78, -33.68) * mm, "end": v(-4.42, -33.85) * mm});
            skLineSegment(sketch, "E168.MirrorCS", {"start": v(-4.05, -34.82) * mm, "end": v(-4.68, -35.18) * mm});
            skLineSegment(sketch, "E169.MirrorCS", {"start": v(-0.24, -28.67) * mm, "end": v(0.5, -28.67) * mm});
            skLineSegment(sketch, "E170.MirrorCS", {"start": v(-0.24, -36.4) * mm, "end": v(0.5, -36.4) * mm});
            skArc(sketch, "E171.MirrorCS", {"start": v(-0.94, -31.28) * mm, "mid": v(-0.45, -30.88) * mm, "end": v(0.14, -30.66) * mm});
            skArc(sketch, "E172.MirrorCS", {"start": v(-4.68, -35.18) * mm, "mid": v(-5.32, -32.53) * mm, "end": v(-4.68, -29.89) * mm});
            skArc(sketch, "E173.MirrorCS", {"start": v(0.2, -37.63) * mm, "mid": v(-0.3, -37.57) * mm, "end": v(-0.81, -37.46) * mm});
            skArc(sketch, "E174.MirrorCS", {"start": v(-3.1, -36.14) * mm, "mid": v(-3.44, -35.76) * mm, "end": v(-3.75, -35.34) * mm});
            skArc(sketch, "E175.MirrorCS", {"start": v(-2.63, -29.4) * mm, "mid": v(-1.71, -28.7) * mm, "end": v(-0.64, -28.25) * mm});
            skArc(sketch, "E176.MirrorCS", {"start": v(-4.05, -34.82) * mm, "mid": v(-4.26, -34.35) * mm, "end": v(-4.42, -33.85) * mm});
            skLineSegment(sketch, "E177.MirrorCS", {"start": v(0.14, -34.41) * mm, "end": v(-0.24, -36.4) * mm});
            skArc(sketch, "E178.MirrorCS", {"start": v(0.14, -34.41) * mm, "mid": v(-0.45, -34.2) * mm, "end": v(-0.94, -33.79) * mm});
            skArc(sketch, "E179.MirrorCS", {"start": v(-3.75, -29.73) * mm, "mid": v(-3.44, -29.31) * mm, "end": v(-3.1, -28.93) * mm});
            skArc(sketch, "E180.MirrorCS", {"start": v(-3.78, -33.68) * mm, "mid": v(-3.93, -32.53) * mm, "end": v(-3.78, -31.39) * mm});
            skArc(sketch, "E181.MirrorCS", {"start": v(-4.38, -29.37) * mm, "mid": v(-2.4, -27.5) * mm, "end": v(0.2, -26.72) * mm});
            skLineSegment(sketch, "E182.MirrorCS", {"start": v(-2.46, -35.12) * mm, "end": v(-0.94, -33.79) * mm});
            skLineSegment(sketch, "E183.MirrorCS", {"start": v(-1.3, -33.16) * mm, "end": v(-3.21, -33.82) * mm});
            skArc(sketch, "E184.MirrorCS", {"start": v(-0.81, -27.6) * mm, "mid": v(-0.3, -27.5) * mm, "end": v(0.2, -27.44) * mm});
            skArc(sketch, "E185.MirrorCS", {"start": v(-0.64, -36.82) * mm, "mid": v(-1.71, -36.38) * mm, "end": v(-2.63, -35.67) * mm});
            skLineSegment(sketch, "E186.MirrorCS", {"start": v(0.14, -30.66) * mm, "end": v(-0.24, -28.67) * mm});
            skLineSegment(sketch, "E187.MirrorCS", {"start": v(-3.21, -33.82) * mm, "end": v(-2.46, -35.12) * mm});
            skArc(sketch, "E188.MirrorCS", {"start": v(-4.42, -31.22) * mm, "mid": v(-4.26, -30.72) * mm, "end": v(-4.05, -30.25) * mm});
            skArc(sketch, "E189.MirrorCS", {"start": v(-1.3, -33.16) * mm, "mid": v(-1.4, -32.53) * mm, "end": v(-1.3, -31.91) * mm});
            skArc(sketch, "E190.MirrorCS", {"start": v(0.2, -38.35) * mm, "mid": v(-2.4, -37.58) * mm, "end": v(-4.38, -35.7) * mm});
            skLineSegment(sketch, "E191.MirrorCS", {"start": v(-1.3, -31.91) * mm, "end": v(-3.21, -31.25) * mm});
            skLineSegment(sketch, "E192.MirrorCS", {"start": v(-0.94, -31.28) * mm, "end": v(-2.46, -29.95) * mm});
            skArc(sketch, "E193.MirrorCS", {"start": v(0.5, -39.03) * mm, "mid": v(-6, -32.53) * mm, "end": v(0.5, -26.03) * mm});
            skSolve(sketch);
        }
        {
            var Q0;
            {var subQ0=sQuery(id+"F0.wireOp",EDGE,"E0.top");Q0=makeQuery(id+"F12.boolean.opBoolean","MERGE",FACE,{"derivedFrom":[makeQuery(id+"F1.opExtrude","SWEPT_FACE",FACE,{"disambiguationData":[OSD([subQ0])]}),makeQuery(id+"F12.opExtrude","CAP_FACE",FACE,{"disambiguationData":[OSD([sQuery(id+"F11.wireOp",EDGE,"E22.1"),sQuery(id+"F11.wireOp",EDGE,"E24"),sQuery(id+"F11.wireOp",EDGE,"E26"),sQuery(id+"F11.wireOp",EDGE,"E27.left"),sQuery(id+"F11.wireOp",EDGE,"E28"),sQuery(id+"F11.wireOp",EDGE,"E31.trimOffspring")])],"isStart":true}),makeQuery(id+"F12.opExtrude","CAP_FACE",FACE,{"disambiguationData":[OSD([sQuery(id+"F11.wireOp",EDGE,"E36.1"),sQuery(id+"F11.wireOp",EDGE,"E38"),sQuery(id+"F11.wireOp",EDGE,"E40"),sQuery(id+"F11.wireOp",EDGE,"E41.left"),sQuery(id+"F11.wireOp",EDGE,"E42"),sQuery(id+"F11.wireOp",EDGE,"E45.trimOffspring")])],"isStart":true}),makeQuery(id+"F12.opExtrude","CAP_FACE",FACE,{"disambiguationData":[OSD([sQuery(id+"F11.wireOp",EDGE,"E50.1"),sQuery(id+"F11.wireOp",EDGE,"E52"),sQuery(id+"F11.wireOp",EDGE,"E54"),sQuery(id+"F11.wireOp",EDGE,"E55.left"),sQuery(id+"F11.wireOp",EDGE,"E56"),sQuery(id+"F11.wireOp",EDGE,"E59.trimOffspring")])],"isStart":true}),makeQuery(id+"F12.opExtrude","CAP_FACE",FACE,{"disambiguationData":[OSD([subQ0,sQuery(id+"F0.wireOp",EDGE,"E0.left"),sQuery(id+"F11.wireOp",EDGE,"E50.2"),sQuery(id+"F11.wireOp",EDGE,"E91")])],"isStart":true}),makeQuery(id+"F12.opExtrude","CAP_FACE",FACE,{"disambiguationData":[OSD([subQ0,sQuery(id+"F0.wireOp",EDGE,"E0.right"),sQuery(id+"F11.wireOp",EDGE,"E64.0"),sQuery(id+"F11.wireOp",EDGE,"E104")])],"isStart":true}),makeQuery(id+"F12.opExtrude","CAP_FACE",FACE,{"disambiguationData":[OSD([sQuery(id+"F11.wireOp",EDGE,"E64.3"),sQuery(id+"F11.wireOp",EDGE,"E66.right"),sQuery(id+"F11.wireOp",EDGE,"E68.bottom"),sQuery(id+"F11.wireOp",EDGE,"E68.top"),sQuery(id+"F11.wireOp",EDGE,"E68.left"),sQuery(id+"F11.wireOp",EDGE,"E69.trimOffspring"),sQuery(id+"F11.wireOp",EDGE,"E71.trimOffspring"),sQuery(id+"F11.wireOp",EDGE,"E72.trimOffspring"),sQuery(id+"F11.wireOp",EDGE,"E73.trimOffspring"),sQuery(id+"F11.wireOp",EDGE,"E74.trimOffspring")])],"isStart":true}),makeQuery(id+"F12.opExtrude","CAP_FACE",FACE,{"disambiguationData":[OSD([sQuery(id+"F11.wireOp",EDGE,"E77.3"),sQuery(id+"F11.wireOp",EDGE,"E79.right"),sQuery(id+"F11.wireOp",EDGE,"E81.bottom"),sQuery(id+"F11.wireOp",EDGE,"E81.top"),sQuery(id+"F11.wireOp",EDGE,"E81.left"),sQuery(id+"F11.wireOp",EDGE,"E82.trimOffspring"),sQuery(id+"F11.wireOp",EDGE,"E84.trimOffspring"),sQuery(id+"F11.wireOp",EDGE,"E85.trimOffspring"),sQuery(id+"F11.wireOp",EDGE,"E86.trimOffspring"),sQuery(id+"F11.wireOp",EDGE,"E87.trimOffspring")])],"isStart":true}),makeQuery(id+"F12.opExtrude","CAP_FACE",FACE,{"disambiguationData":[OSD([sQuery(id+"F11.wireOp",EDGE,"E90.3"),sQuery(id+"F11.wireOp",EDGE,"E93.right"),sQuery(id+"F11.wireOp",EDGE,"E95.bottom"),sQuery(id+"F11.wireOp",EDGE,"E95.top"),sQuery(id+"F11.wireOp",EDGE,"E95.left"),sQuery(id+"F11.wireOp",EDGE,"E96.trimOffspring"),sQuery(id+"F11.wireOp",EDGE,"E98.trimOffspring"),sQuery(id+"F11.wireOp",EDGE,"E99.trimOffspring"),sQuery(id+"F11.wireOp",EDGE,"E100.trimOffspring"),sQuery(id+"F11.wireOp",EDGE,"E101.trimOffspring")])],"isStart":true})]});}
            var sketch = newSketch(context, id + "F14", { "sketchPlane" : qUnion([Q0])});
            skPoint(sketch, "E194.0", {"position": v(-13.03, 37.85) * mm});
            skPoint(sketch, "E195.0", {"position": v(12.02, 35.02) * mm});
            skPoint(sketch, "E196", {"position": v(-12.03, 34.02) * mm});
            skLineSegment(sketch, "E197", {"start": v(-0.5, 29.5) * mm, "end": v(-0.5, 28.05) * mm});
            skPoint(sketch, "E198", {"position": v(-12.03, 28.05) * mm});
            skPoint(sketch, "E199", {"position": v(11.02, 28.05) * mm});
            skPoint(sketch, "E200", {"position": v(11.02, 29.5) * mm});
            skPoint(sketch, "E201", {"position": v(-12.03, 29.5) * mm});
            skPoint(sketch, "E202", {"position": v(11.02, 34.02) * mm});
            skPoint(sketch, "E203", {"position": v(-12.03, 23.52) * mm});
            skPoint(sketch, "E204", {"position": v(11.02, 23.52) * mm});
            skText(sketch, "E205", { "text": "Fighter", "fontName": "NotoSans-Bold.ttf"});
            skPoint(sketch, "E206", {"position": v(-0.5, 34.02) * mm});
            skText(sketch, "E207", { "text": "TIE", "fontName": "NotoSans-Bold.ttf"});
            skPoint(sketch, "E208.0", {"position": v(12.02, 16.7) * mm});
            skLineSegment(sketch, "E209.0", {"start": v(12.02, 37.85) * mm, "end": v(12.02, 19.7) * mm});
            skPoint(sketch, "E210.0", {"position": v(-0.5, 19.7) * mm});
            const initialGuessF14  = {"E205": [-0.01203, 0.02352, 1, 0, 0.00453], "E207": [-0.00533, 0.0295, 1, 0, 0.00452]};
            skSetInitialGuess(sketch, initialGuessF14);
            skSolve(sketch);
        }
        {
            var Q0;
            Q0 = qSketchRegion(id + "F14", true);
            var Q1;
            Q1=makeQuery(id+"F13.imprint","IMPRINT",FACE,{"disambiguationData":[TD([[makeQuery(id+"F13.imprint","IMPRINT",EDGE,{"derivedFrom":sQuery(id+"F13.wireOp",EDGE,"E112")}),1.0]])]});
            extrude(context, id + "F15", {"entities" : qUnion([Q0, Q1]), "operationType" : NewBodyOperationType.REMOVE, "oppositeDirection" : true, "depth" : 1 * mm, "offsetDistance" : 25 * mm});
        }
    });
